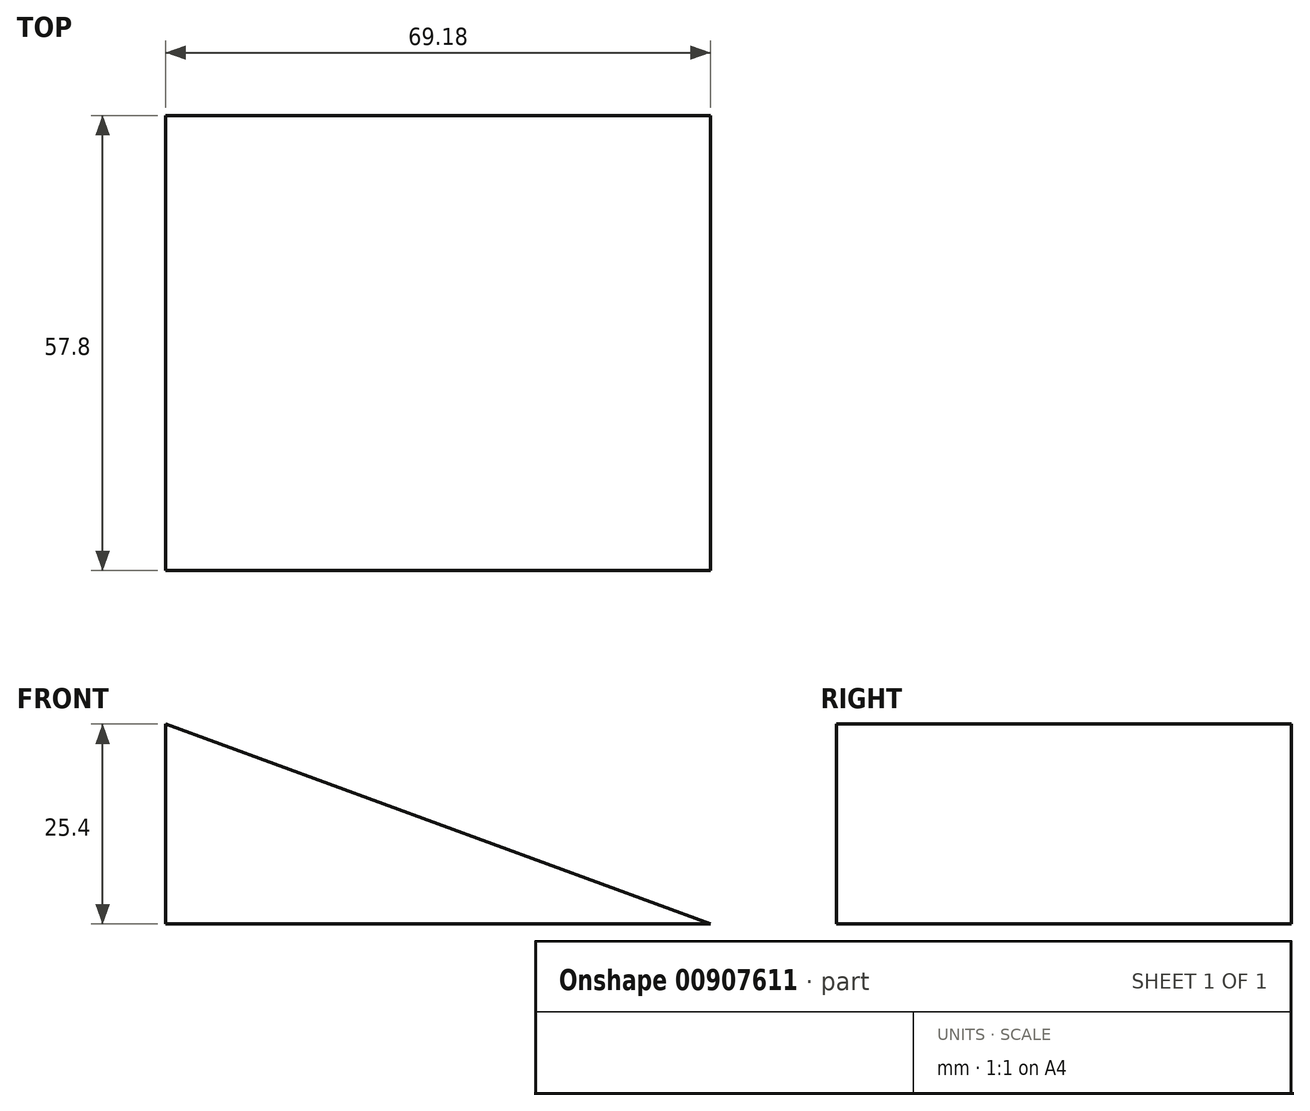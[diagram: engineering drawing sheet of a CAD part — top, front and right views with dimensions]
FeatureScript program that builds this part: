
annotation { "Feature Type Name" : "Feature", "Feature Type Description" : "" }
export const myFeature = defineFeature(function(context is Context, id is Id, definition is map)
    precondition{}
    {
        {
            var Q0;
            Q0=qCreatedBy(makeId("Top.planeOp"),FACE);
            var sketch = newSketch(context, id + "F0", { "sketchPlane" : qUnion([Q0])});
            skLineSegment(sketch, "E0.bottom", {"start": v(-40.42, -29.42) * mm, "end": v(28.76, -29.42) * mm});
            skLineSegment(sketch, "E0.top", {"start": v(-40.42, 28.38) * mm, "end": v(28.76, 28.38) * mm});
            skLineSegment(sketch, "E0.left", {"start": v(-40.42, -29.42) * mm, "end": v(-40.42, 28.38) * mm});
            skLineSegment(sketch, "E0.right", {"start": v(28.76, -29.42) * mm, "end": v(28.76, 28.38) * mm});
            skSolve(sketch);
        }
        {
            var Q0;
            Q0=makeQuery(id+"F0.imprint","IMPRINT",FACE,{"disambiguationData":[TD([[makeQuery(id+"F0.imprint","IMPRINT",EDGE,{"derivedFrom":sQuery(id+"F0.wireOp",EDGE,"E0.bottom")}),1.0]])]});
            extrude(context, id + "F1", {"entities" : qUnion([Q0]), "depth" : 25.4 * mm, "offsetDistance" : 25.4 * mm});
        }
        {
            var Q0;
            Q0=makeQuery(id+"F1.opExtrude","SWEPT_FACE",FACE,{"disambiguationData":[OSD([sQuery(id+"F0.wireOp",EDGE,"E0.bottom")])]});
            var sketch = newSketch(context, id + "F2", { "sketchPlane" : qUnion([Q0])});
            skLineSegment(sketch, "E1", {"start": v(-40.42, 25.4) * mm, "end": v(28.76, 0) * mm});
            skLineSegment(sketch, "E2", {"start": v(28.76, 25.4) * mm, "end": v(-40.42, 25.4) * mm});
            skSolve(sketch);
        }
        {
            var Q0;
            Q0=makeQuery(id+"F2.imprint","IMPRINT",FACE,{"disambiguationData":[TD([[makeQuery(id+"F2.imprint","IMPRINT",EDGE,{"derivedFrom":sQuery(id+"F2.wireOp",EDGE,"E1")}),1.0]])]});
            extrude(context, id + "F3", {"entities" : qUnion([Q0]), "operationType" : NewBodyOperationType.REMOVE, "endBound" : BoundingType.UP_TO_NEXT, "oppositeDirection" : true, "depth" : 25.4 * mm, "offsetDistance" : 25.4 * mm});
        }
        {
            var Q0;
            Q0=makeQuery(id+"F3.boolean.opBoolean","COPY",FACE,{"derivedFrom":makeQuery(id+"F3.opExtrude","SWEPT_FACE",FACE,{"disambiguationData":[OSD([sQuery(id+"F2.wireOp",EDGE,"E1")])]})});
            var sketch = newSketch(context, id + "F4", { "sketchPlane" : qUnion([Q0])});
            skCircle(sketch, "E3", {"center": v(-28.78, -12.4) * mm, "radius": 6.48 * mm});
            skSolve(sketch);
        }
        {
            var Q0;
            Q0=sQuery(id+"F4.wireOp",EDGE,"E3");
            extrude(context, id + "F5", {"bodyType" : ToolBodyType.SURFACE, "surfaceEntities" : qUnion([Q0]), "depth" : 25.4 * mm, "offsetDistance" : 25.4 * mm});
        }
    });
